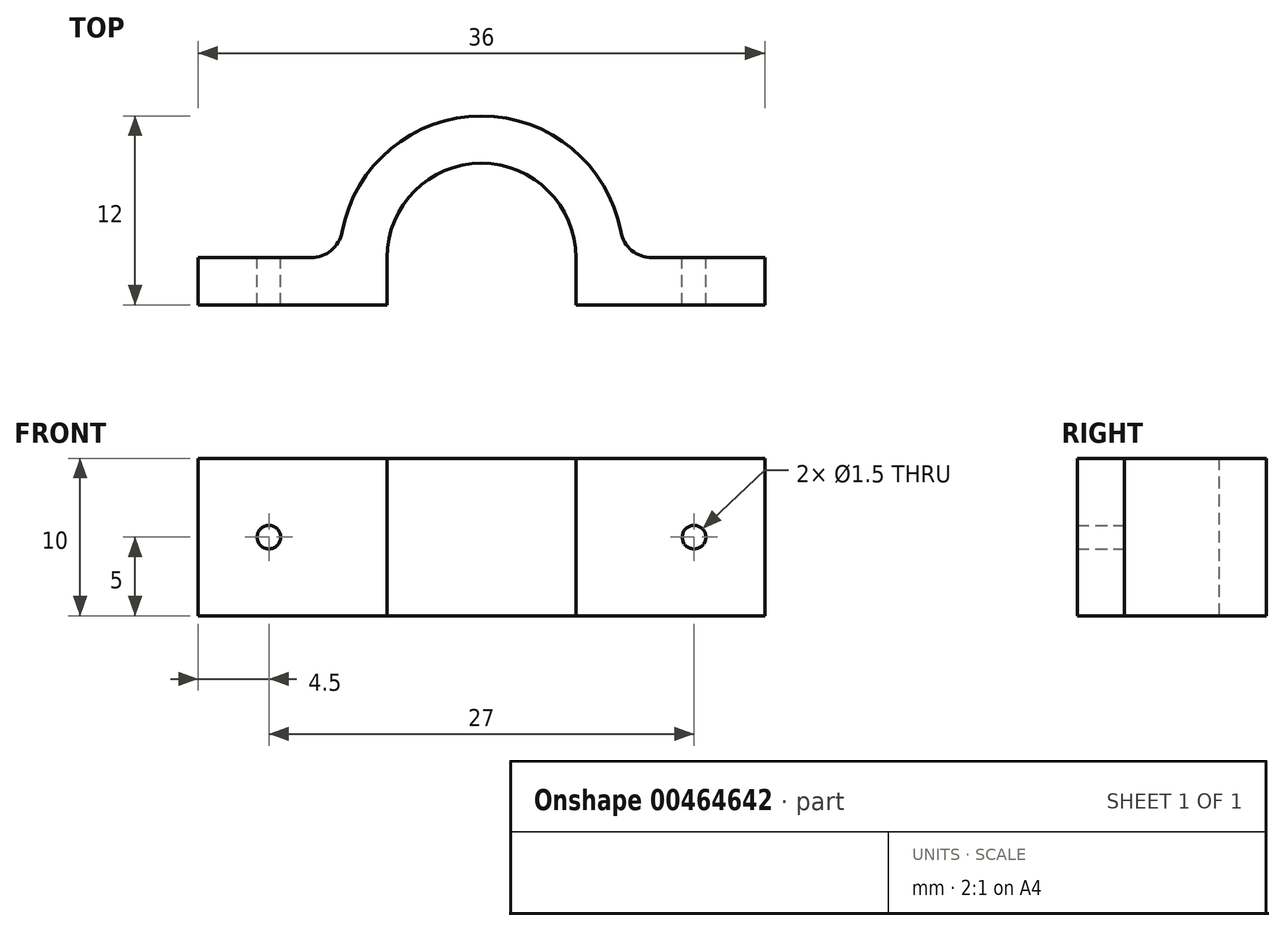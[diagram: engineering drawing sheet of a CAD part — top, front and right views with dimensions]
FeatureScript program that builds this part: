
annotation { "Feature Type Name" : "Feature", "Feature Type Description" : "" }
export const myFeature = defineFeature(function(context is Context, id is Id, definition is map)
    precondition{}
    {
        {
            var Q0;
            Q0=qCreatedBy(makeId("Top.planeOp"),FACE);
            var sketch = newSketch(context, id + "F0", { "sketchPlane" : qUnion([Q0])});
            skArc(sketch, "E0", {"start": v(6, 0) * mm, "mid": v(0, 6) * mm, "end": v(-6, 0) * mm});
            skArc(sketch, "E1.0", {"start": v(9, 0) * mm, "mid": v(0, 9) * mm, "end": v(-9, 0) * mm});
            skLineSegment(sketch, "E2.bottom", {"start": v(9, 0) * mm, "end": v(18, 0) * mm});
            skLineSegment(sketch, "E2.top", {"start": v(6, -3) * mm, "end": v(18, -3) * mm});
            skLineSegment(sketch, "E2.right", {"start": v(18, 0) * mm, "end": v(18, -3) * mm});
            skLineSegment(sketch, "E3.bottom", {"start": v(-9, 0) * mm, "end": v(-18, 0) * mm});
            skLineSegment(sketch, "E3.top", {"start": v(-6, -3) * mm, "end": v(-18, -3) * mm});
            skLineSegment(sketch, "E3.right", {"start": v(-18, 0) * mm, "end": v(-18, -3) * mm});
            skLineSegment(sketch, "E4", {"start": v(-6, 0) * mm, "end": v(-6, -3) * mm});
            skLineSegment(sketch, "E5", {"start": v(6, 0) * mm, "end": v(6, -3) * mm});
            skPoint(sketch, "E6.orphan", {"position": v(0, -3) * mm});
            skSolve(sketch);
        }
        {
            var Q0;
            Q0=makeQuery(id+"F0.imprint","IMPRINT",FACE,{"disambiguationData":[TD([[makeQuery(id+"F0.imprint","IMPRINT",EDGE,{"derivedFrom":sQuery(id+"F0.wireOp",EDGE,"E0")}),-1.0]])]});
            extrude(context, id + "F1", {"entities" : qUnion([Q0]), "depth" : 10 * mm});
        }
        {
            var Q0;
            Q0=makeQuery(id+"F1.opExtrude","SWEPT_FACE",FACE,{"disambiguationData":[OSD([sQuery(id+"F0.wireOp",EDGE,"E2.bottom")])]});
            var sketch = newSketch(context, id + "F2", { "sketchPlane" : qUnion([Q0])});
            skLineSegment(sketch, "E7", {"start": v(-17, 10) * mm, "end": v(-17, 0) * mm, "construction": true});
            skLineSegment(sketch, "E8", {"start": v(-9, 5) * mm, "end": v(-18, 5) * mm, "construction": true});
            skPoint(sketch, "E9", {"position": v(-13.5, 5) * mm});
            skLineSegment(sketch, "E10", {"start": v(0, 0) * mm, "end": v(0, 20.25) * mm, "construction": true});
            skPoint(sketch, "E11.MirrorP", {"position": v(13.5, 5) * mm});
            skSolve(sketch);
        }
        {
            var Q0;
            Q0=sQuery(id+"F2.wireOp",VERTEX,"E9");
            var Q1;
            Q1=sQuery(id+"F2.wireOp",VERTEX,"E11.MirrorP");
            var Q2;
            Q2=makeQuery(id+"F1.opExtrude","SWEPT_BODY",BODY,{"disambiguationData":[OSD([sQuery(id+"F0.wireOp",EDGE,"E0"),sQuery(id+"F0.wireOp",EDGE,"E1.0"),sQuery(id+"F0.wireOp",EDGE,"E2.bottom"),sQuery(id+"F0.wireOp",EDGE,"E2.top"),sQuery(id+"F0.wireOp",EDGE,"E2.right"),sQuery(id+"F0.wireOp",EDGE,"E3.bottom"),sQuery(id+"F0.wireOp",EDGE,"E3.top"),sQuery(id+"F0.wireOp",EDGE,"E3.right"),sQuery(id+"F0.wireOp",EDGE,"E4"),sQuery(id+"F0.wireOp",EDGE,"E5")])]});
            hole(context, id + "F3", {"style" : HoleStyle.SIMPLE, "endStyle" : HoleEndStyle.THROUGH, "holeDiameter" : 1.5 * mm, "isTappedThrough" : true, "tappedDepth" : 12 * mm, "tapClearance" : 3, "startFromSketch" : true, "locations" : qUnion([Q0, Q1]), "scope" : qUnion([Q2])});
        }
        {
            var Q0;
            Q0=makeQuery(id+"F1.opExtrude","SWEPT_EDGE",EDGE,{"disambiguationData":[OSD([sQuery(id+"F0.wireOp",EDGE,"E1.0"),sQuery(id+"F0.wireOp",EDGE,"E2.bottom")])]});
            var Q1;
            Q1=makeQuery(id+"F1.opExtrude","SWEPT_EDGE",EDGE,{"disambiguationData":[OSD([sQuery(id+"F0.wireOp",EDGE,"E1.0"),sQuery(id+"F0.wireOp",EDGE,"E3.bottom")])]});
            fillet(context, id + "F4", {"entities" : qUnion([Q0, Q1]), "radius" : 2 * mm, "tangentPropagation" : true, "allowEdgeOverflow" : false});
        }
    });
